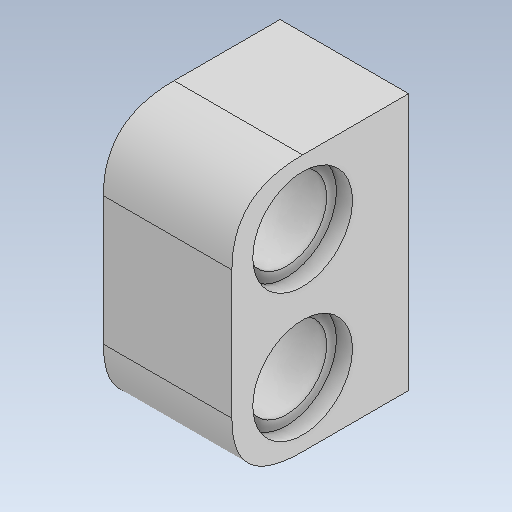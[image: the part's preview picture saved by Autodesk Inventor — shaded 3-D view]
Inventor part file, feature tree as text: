
AUTODESK INVENTOR PART (.ipt)
format: ipt  version: 2020 (Build 240168000, 168)  size: 159,232 bytes
history: native  units: mm
features: sketch x5, other x4, extrude x1
ambient origin geometry x8: Origin, YZ Plane, XZ Plane, XY Plane, X Axis, Y Axis, Z Axis, Center Point
bodies: Body1 (feature_tree)
feature tree (10):
  other  "apoio_array.ipt"
  extrude  "Extrusão1"  Depth=10.0mm TaperAngle=0.0deg
  other  "Sólido1::apoio_array.ipt"
  other  "OperaçãoIdentificador1"
  sketch  "Esboço1"  dims[d0=10.0mm d1=3.0mm d2=0.0mm]
  sketch  "Esboço3"
  sketch  "Esboço4"
  sketch  "Esboço5"
  sketch  "Esboço6"
  other  "Sólido1"
